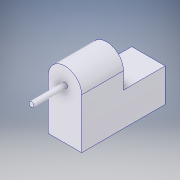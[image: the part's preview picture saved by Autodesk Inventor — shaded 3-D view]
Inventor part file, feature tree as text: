
AUTODESK INVENTOR PART (.ipt)
format: ipt  version: 2018 (Build 220112000, 112)  size: 107,008 bytes
history: native  units: in
note: dims shown in document units (in); Inventor stores cm internally (conversion verified against a paired STEP export)
features: extrude x2, sketch x2, fillet x1
ambient origin geometry x8: Origin, YZ Plane, XZ Plane, XY Plane, X Axis, Y Axis, Z Axis, Center Point
bodies: Solid1 (feature_tree)
feature tree (5):
  extrude  "Extrusion1"  Depth=0.3937in
  fillet  "Fillet1"  Radius=0.1181in
  extrude  "Extrusion2"  [1 undecoded]
  sketch  "Sketch1"  dims[d2=0.7874in d3=0.0in d4=0.3937in d5=0.1181in]
  sketch  "Sketch3"  dims[d6=0.7874in d7=0.0in]
note: 1 required parameter value undecoded (feature->parameter linkage not recoverable at this tier; creation-order binding heuristic only, values carry confidence <= 0.55)
